# Revit family: Titan 150W
name_source: partatom
category: Lighting Fixtures
revit_build: Autodesk Revit 2015 (Build: 20140322_1515(x64)
units: mm (PartAtom-declared; Revit-internal decimal feet)

## types (2) — shared parameters
Beam Angle = 90°
CRI = 80
Casing Color = Black
Color Temperature = 4000K
Cutout = -
Default Elevation = 1219 mm
Depth = -
Description = Floodlight
Dimensions = 370mm x 275mm x 110mm
Directivity = No
Driver = Integrated
Housing Material = Aluminium
IP Code = IP65, IK10
Lamp = LED
Last Updated = 22.2.2017
Lifetime L70 = 50000h
Lumens Output = 18900lm
Manufacturer = Winled Oy Ltd
Model = Titan 150W
Operating Temperature Range = -30 to +50°C
Type Image = Titan 150W.png
URL = www.winled.fi
Voltage = 230 V
Wattage Comments = 150W

## per-type parameters (varying)
| type | Dimmable | Product Number |
| Titan 150W, 230V - 67TE395N150R | No | 67TE395N150R |
| Titan 150W, 1-10V, 230V - 67TE395N150R10 | Yes | 67TE395N150R10 |

## geometry (parser evidence)
native form markers: Sweep x9
no freeform markers — native parametric forms only
